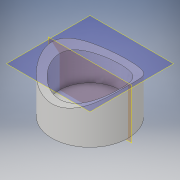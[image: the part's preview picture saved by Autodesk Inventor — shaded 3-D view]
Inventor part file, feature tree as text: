
AUTODESK INVENTOR PART (.ipt)
format: ipt  version: 2018 (Build 220112000, 112)  size: 121,856 bytes
history: native  units: in
note: dims shown in document units (in); Inventor stores cm internally (conversion verified against a paired STEP export)
features: sketch x3, extrude x3, plane x1
ambient origin geometry x8: Origin, YZ Plane, XZ Plane, XY Plane, X Axis, Y Axis, Z Axis, Center Point
bodies: Solid1 (feature_tree)
feature tree (7):
  sketch  "Sketch1"  dims[d0=0.5in d1=0.3in d2=0.0in]
  extrude  "Extrusion1"  Depth=0.3in TaperAngle=0.0deg
  extrude  "Extrusion2"  Depth=0.35in
  plane  "Work Plane1"
  extrude  "Extrusion3"  [1 undecoded]
  sketch  "Sketch2"  dims[d5=0.1in d6=0.35in]
  sketch  "Sketch3"  dims[d7=1.0in d8=0.0in d9=-0.3in d10=0.4in d11=0.25in d12=0.0in]
note: 1 required parameter value undecoded (feature->parameter linkage not recoverable at this tier; creation-order binding heuristic only, values carry confidence <= 0.55)
